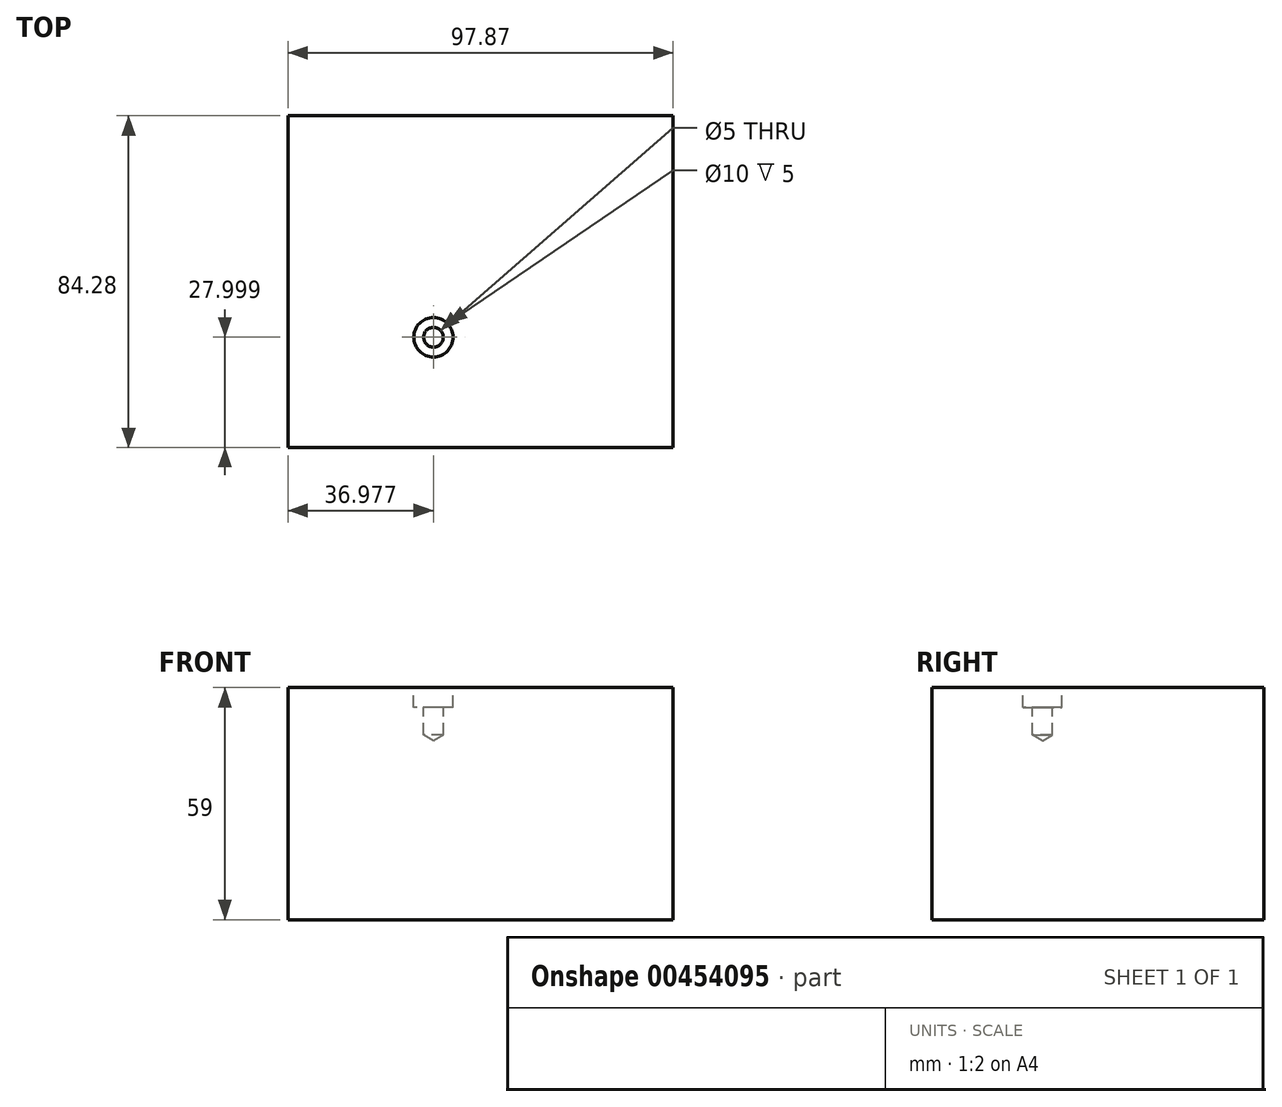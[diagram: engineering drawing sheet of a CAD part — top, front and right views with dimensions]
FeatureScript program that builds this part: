
annotation { "Feature Type Name" : "Feature", "Feature Type Description" : "" }
export const myFeature = defineFeature(function(context is Context, id is Id, definition is map)
    precondition{}
    {
        {
            var Q0;
            Q0=qCreatedBy(makeId("Top.planeOp"),FACE);
            var sketch = newSketch(context, id + "F0", { "sketchPlane" : qUnion([Q0])});
            skLineSegment(sketch, "E0.bottom", {"start": v(-56.3, 43.74) * mm, "end": v(41.56, 43.74) * mm});
            skLineSegment(sketch, "E0.top", {"start": v(-56.3, -40.54) * mm, "end": v(41.56, -40.54) * mm});
            skLineSegment(sketch, "E0.left", {"start": v(-56.3, 43.74) * mm, "end": v(-56.3, -40.54) * mm});
            skLineSegment(sketch, "E0.right", {"start": v(41.56, 43.74) * mm, "end": v(41.56, -40.54) * mm});
            skSolve(sketch);
        }
        {
            var Q0;
            Q0=makeQuery(id+"F0.imprint","IMPRINT",FACE,{"disambiguationData":[TD([[makeQuery(id+"F0.imprint","IMPRINT",EDGE,{"derivedFrom":sQuery(id+"F0.wireOp",EDGE,"E0.bottom")}),-1.0]])]});
            extrude(context, id + "F1", {"entities" : qUnion([Q0]), "depth" : 59 * mm});
        }
        {
            var Q0;
            Q0=makeQuery(id+"F1.opExtrude","CAP_FACE",FACE,{"disambiguationData":[OSD([sQuery(id+"F0.wireOp",EDGE,"E0.bottom"),sQuery(id+"F0.wireOp",EDGE,"E0.top"),sQuery(id+"F0.wireOp",EDGE,"E0.left"),sQuery(id+"F0.wireOp",EDGE,"E0.right")])],"isStart":false});
            var sketch = newSketch(context, id + "F2", { "sketchPlane" : qUnion([Q0])});
            skFitSpline(sketch, "E1", {"points": [v(-56.3, -23.96) * mm, v(-19.33, -12.54) * mm, v(-10.63, 13.56) * mm, v(41.56, 21.17) * mm], "startDerivative": vector(140.37, 13.22) * mm, "endDerivative": vector(171.77, -6.9) * mm});
            skFitSpline(sketch, "E2", {"points": [v(-56.3, 18.86) * mm, v(-24.15, 25.9) * mm, v(7.04, 36.18) * mm, v(41.56, 32.63) * mm], "startDerivative": vector(98.53, 15.89) * mm, "endDerivative": vector(103.87, -22.34) * mm});
            skSolve(sketch);
        }
        {
            var Q0;
            Q0=sQuery(id+"F2.wireOp",VERTEX,"E1.1.internal");
            var Q1;
            Q1=makeQuery(id+"F1.opExtrude","SWEPT_BODY",BODY,{"disambiguationData":[OSD([sQuery(id+"F0.wireOp",EDGE,"E0.bottom"),sQuery(id+"F0.wireOp",EDGE,"E0.top"),sQuery(id+"F0.wireOp",EDGE,"E0.left"),sQuery(id+"F0.wireOp",EDGE,"E0.right")])]});
            hole(context, id + "F3", {"style" : HoleStyle.C_BORE, "endStyle" : HoleEndStyle.BLIND, "holeDiameter" : 5 * mm, "cBoreDiameter" : 10 * mm, "cBoreDepth" : 5 * mm, "holeDepth" : 12 * mm, "isTappedThrough" : true, "tappedDepth" : 12 * mm, "tapClearance" : 3, "startFromSketch" : true, "locations" : qUnion([Q0]), "scope" : qUnion([Q1])});
        }
    });
